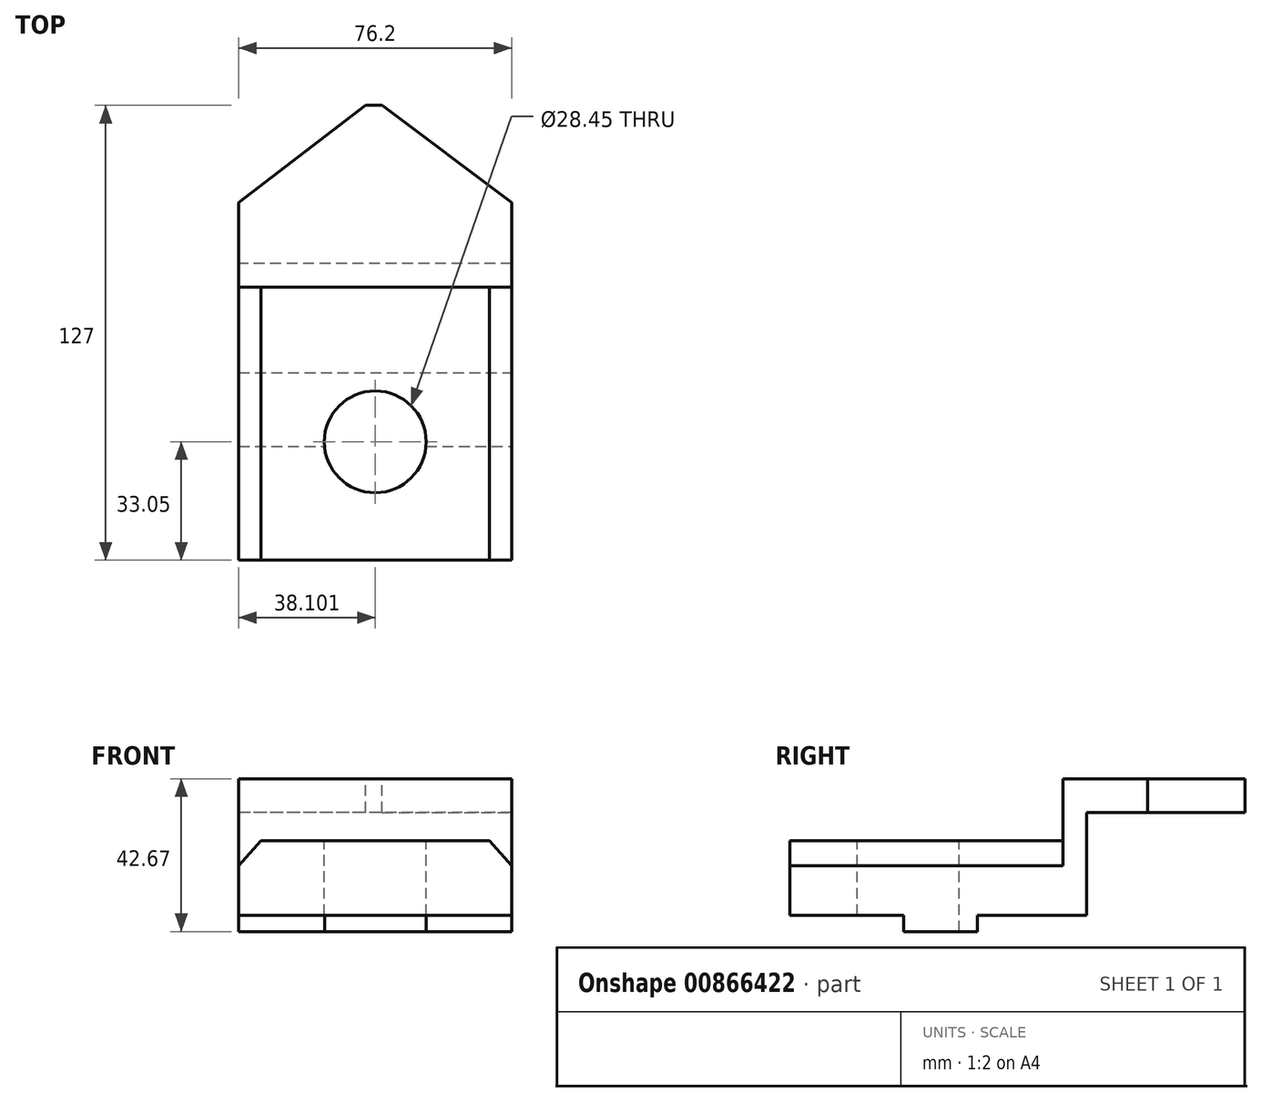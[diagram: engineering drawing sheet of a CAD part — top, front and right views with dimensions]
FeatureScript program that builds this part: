
annotation { "Feature Type Name" : "Feature", "Feature Type Description" : "" }
export const myFeature = defineFeature(function(context is Context, id is Id, definition is map)
    precondition{}
    {
        {
            var Q0;
            Q0=qCreatedBy(makeId("Top.planeOp"),FACE);
            var sketch = newSketch(context, id + "F0", { "sketchPlane" : qUnion([Q0])});
            skLineSegment(sketch, "E0.bottom", {"start": v(-35.48, 29.63) * mm, "end": v(40.72, 29.63) * mm});
            skLineSegment(sketch, "E0.left", {"start": v(-35.48, 29.63) * mm, "end": v(-35.48, -46.57) * mm});
            skLineSegment(sketch, "E0.right", {"start": v(40.72, 29.63) * mm, "end": v(40.72, -46.57) * mm});
            skLineSegment(sketch, "E1.bottom", {"start": v(-35.48, -46.57) * mm, "end": v(40.72, -46.57) * mm});
            skLineSegment(sketch, "E2", {"start": v(-35.48, 29.63) * mm, "end": v(-35.48, 80.43) * mm});
            skLineSegment(sketch, "E3", {"start": v(-35.48, 80.43) * mm, "end": v(40.72, 80.43) * mm});
            skLineSegment(sketch, "E4", {"start": v(40.72, 80.43) * mm, "end": v(40.72, 29.63) * mm});
            skSolve(sketch);
        }
        {
            var Q0;
            {var subQ0=sQuery(id+"F0.wireOp",EDGE,"E0.bottom");Q0=makeQuery(id+"F0.imprint","IMPRINT",FACE,{"disambiguationData":[TD([[makeQuery(id+"F0.imprint","IMPRINT",EDGE,{"derivedFrom":subQ0}),-1.0]])]});}
            extrude(context, id + "F1", {"entities" : qUnion([Q0]), "depth" : 25.4 * mm, "offsetDistance" : 25.4 * mm});
        }
        {
            var Q0;
            Q0=makeQuery(id+"F0.imprint","IMPRINT",FACE,{"disambiguationData":[TD([[makeQuery(id+"F0.imprint","IMPRINT",EDGE,{"derivedFrom":sQuery(id+"F0.wireOp",EDGE,"E0.bottom")}),1.0]])]});
            extrude(context, id + "F2", {"entities" : qUnion([Q0]), "operationType" : NewBodyOperationType.ADD, "depth" : 42.67 * mm, "offsetDistance" : 25.4 * mm});
        }
        {
            var Q0;
            Q0=makeQuery(id+"F1.opExtrude","SWEPT_FACE",FACE,{"disambiguationData":[OSD([sQuery(id+"F0.wireOp",EDGE,"E1.bottom")])]});
            var sketch = newSketch(context, id + "F3", { "sketchPlane" : qUnion([Q0])});
            skLineSegment(sketch, "E5", {"start": v(-29.25, 25.4) * mm, "end": v(-35.48, 18.37) * mm});
            skLineSegment(sketch, "E6", {"start": v(34.49, 25.4) * mm, "end": v(40.72, 18.37) * mm});
            skSolve(sketch);
        }
        {
            var Q0;
            {var subQ0=sQuery(id+"F3.wireOp",EDGE,"E6");Q0=makeQuery(id+"F3.imprint","IMPRINT",FACE,{"disambiguationData":[TD([[makeQuery(id+"F3.imprint","IMPRINT",EDGE,{"derivedFrom":subQ0}),1.0]])]});}
            var Q1;
            {var subQ0=sQuery(id+"F3.wireOp",EDGE,"E5");Q1=makeQuery(id+"F3.imprint","IMPRINT",FACE,{"disambiguationData":[TD([[makeQuery(id+"F3.imprint","IMPRINT",EDGE,{"derivedFrom":subQ0}),-1.0]])]});}
            extrude(context, id + "F4", {"entities" : qUnion([Q0, Q1]), "operationType" : NewBodyOperationType.REMOVE, "oppositeDirection" : true, "depth" : 76.2 * mm, "offsetDistance" : 25.4 * mm});
        }
        {
            var Q0;
            Q0=makeQuery(id+"F1.opExtrude","CAP_FACE",FACE,{"disambiguationData":[OSD([sQuery(id+"F0.wireOp",EDGE,"E0.bottom"),sQuery(id+"F0.wireOp",EDGE,"E0.left"),sQuery(id+"F0.wireOp",EDGE,"E0.right"),sQuery(id+"F0.wireOp",EDGE,"E1.bottom")])],"isStart":false});
            var sketch = newSketch(context, id + "F5", { "sketchPlane" : qUnion([Q0])});
            skCircle(sketch, "E7", {"center": v(2.62, -13.52) * mm, "radius": 14.22 * mm});
            skSolve(sketch);
        }
        {
            var Q0;
            Q0=makeQuery(id+"F5.imprint","IMPRINT",FACE,{"disambiguationData":[TD([[makeQuery(id+"F5.imprint","IMPRINT",EDGE,{"derivedFrom":sQuery(id+"F5.wireOp",EDGE,"E7")}),1.0]])]});
            extrude(context, id + "F6", {"entities" : qUnion([Q0]), "operationType" : NewBodyOperationType.REMOVE, "oppositeDirection" : true, "depth" : 25.4 * mm, "offsetDistance" : 25.4 * mm});
        }
        {
            var Q0;
            Q0=makeQuery(id+"F2.boolean.opBoolean","MERGE",FACE,{"derivedFrom":[makeQuery(id+"F1.opExtrude","SWEPT_FACE",FACE,{"disambiguationData":[OSD([sQuery(id+"F0.wireOp",EDGE,"E0.right")])]}),makeQuery(id+"F2.opExtrude","SWEPT_FACE",FACE,{"disambiguationData":[OSD([sQuery(id+"F0.wireOp",EDGE,"E4")])]})]});
            var sketch = newSketch(context, id + "F7", { "sketchPlane" : qUnion([Q0])});
            skLineSegment(sketch, "E8", {"start": v(-14.82, 0) * mm, "end": v(5.75, 0) * mm});
            skLineSegment(sketch, "E9", {"start": v(-14.82, 0) * mm, "end": v(-14.82, 4.57) * mm});
            skLineSegment(sketch, "E10", {"start": v(-14.82, 4.57) * mm, "end": v(5.75, 4.57) * mm});
            skLineSegment(sketch, "E11", {"start": v(5.75, 4.57) * mm, "end": v(5.75, 0) * mm});
            skLineSegment(sketch, "E12", {"start": v(5.75, 4.57) * mm, "end": v(80.43, 4.57) * mm});
            skLineSegment(sketch, "E13", {"start": v(-14.82, 4.57) * mm, "end": v(-46.57, 4.57) * mm});
            skSolve(sketch);
        }
        {
            var Q0;
            {var subQ0=sQuery(id+"F7.wireOp",EDGE,"E9");Q0=makeQuery(id+"F7.imprint","IMPRINT",FACE,{"disambiguationData":[TD([[makeQuery(id+"F7.imprint","IMPRINT",EDGE,{"derivedFrom":subQ0}),1.0]])]});}
            var Q1;
            {var subQ0=sQuery(id+"F7.wireOp",EDGE,"E11");Q1=makeQuery(id+"F7.imprint","IMPRINT",FACE,{"disambiguationData":[TD([[makeQuery(id+"F7.imprint","IMPRINT",EDGE,{"derivedFrom":subQ0}),1.0]])]});}
            extrude(context, id + "F8", {"entities" : qUnion([Q0, Q1]), "operationType" : NewBodyOperationType.REMOVE, "oppositeDirection" : true, "depth" : 96.27 * mm, "offsetDistance" : 25.4 * mm});
        }
        {
            var Q0;
            Q0=makeQuery(id+"F2.opExtrude","CAP_FACE",FACE,{"disambiguationData":[OSD([sQuery(id+"F0.wireOp",EDGE,"E0.bottom"),sQuery(id+"F0.wireOp",EDGE,"E2"),sQuery(id+"F0.wireOp",EDGE,"E3"),sQuery(id+"F0.wireOp",EDGE,"E4")])],"isStart":false});
            var sketch = newSketch(context, id + "F9", { "sketchPlane" : qUnion([Q0])});
            skLineSegment(sketch, "E14", {"start": v(-35.48, 29.63) * mm, "end": v(-35.48, 53.25) * mm});
            skLineSegment(sketch, "E15", {"start": v(40.72, 29.63) * mm, "end": v(40.72, 53.25) * mm});
            skLineSegment(sketch, "E16", {"start": v(40.72, 53.25) * mm, "end": v(4.57, 80.43) * mm});
            skLineSegment(sketch, "E17", {"start": v(-35.48, 53.25) * mm, "end": v(0, 80.43) * mm});
            skLineSegment(sketch, "E18", {"start": v(0, 80.43) * mm, "end": v(4.57, 80.43) * mm});
            skSolve(sketch);
        }
        {
            var Q0;
            Q0=makeQuery(id+"F2.opExtrude","SWEPT_FACE",FACE,{"disambiguationData":[OSD([sQuery(id+"F0.wireOp",EDGE,"E3")])]});
            var sketch = newSketch(context, id + "F10", { "sketchPlane" : qUnion([Q0])});
            skLineSegment(sketch, "E19.bottom", {"start": v(-40.72, 42.67) * mm, "end": v(35.48, 42.67) * mm});
            skLineSegment(sketch, "E19.top", {"start": v(-40.72, 33.27) * mm, "end": v(35.48, 33.27) * mm});
            skLineSegment(sketch, "E19.left", {"start": v(-40.72, 42.67) * mm, "end": v(-40.72, 33.27) * mm});
            skLineSegment(sketch, "E19.right", {"start": v(35.48, 42.67) * mm, "end": v(35.48, 33.27) * mm});
            skSolve(sketch);
        }
        {
            var Q0;
            {var subQ0=sQuery(id+"F10.wireOp",EDGE,"E19.top");Q0=makeQuery(id+"F10.imprint","IMPRINT",FACE,{"disambiguationData":[TD([[makeQuery(id+"F10.imprint","IMPRINT",EDGE,{"derivedFrom":subQ0}),-1.0]])]});}
            extrude(context, id + "F11", {"entities" : qUnion([Q0]), "operationType" : NewBodyOperationType.REMOVE, "oppositeDirection" : true, "depth" : 44.2 * mm, "offsetDistance" : 25.4 * mm});
        }
        {
            var Q0;
            {var subQ0=sQuery(id+"F9.wireOp",EDGE,"E16");Q0=makeQuery(id+"F9.imprint","IMPRINT",FACE,{"disambiguationData":[TD([[makeQuery(id+"F9.imprint","IMPRINT",EDGE,{"derivedFrom":subQ0}),-1.0]])]});}
            var Q1;
            {var subQ0=sQuery(id+"F9.wireOp",EDGE,"E17");Q1=makeQuery(id+"F9.imprint","IMPRINT",FACE,{"disambiguationData":[TD([[makeQuery(id+"F9.imprint","IMPRINT",EDGE,{"derivedFrom":subQ0}),1.0]])]});}
            extrude(context, id + "F12", {"entities" : qUnion([Q0, Q1]), "operationType" : NewBodyOperationType.REMOVE, "oppositeDirection" : true, "depth" : 25.4 * mm, "offsetDistance" : 25.4 * mm});
        }
    });
